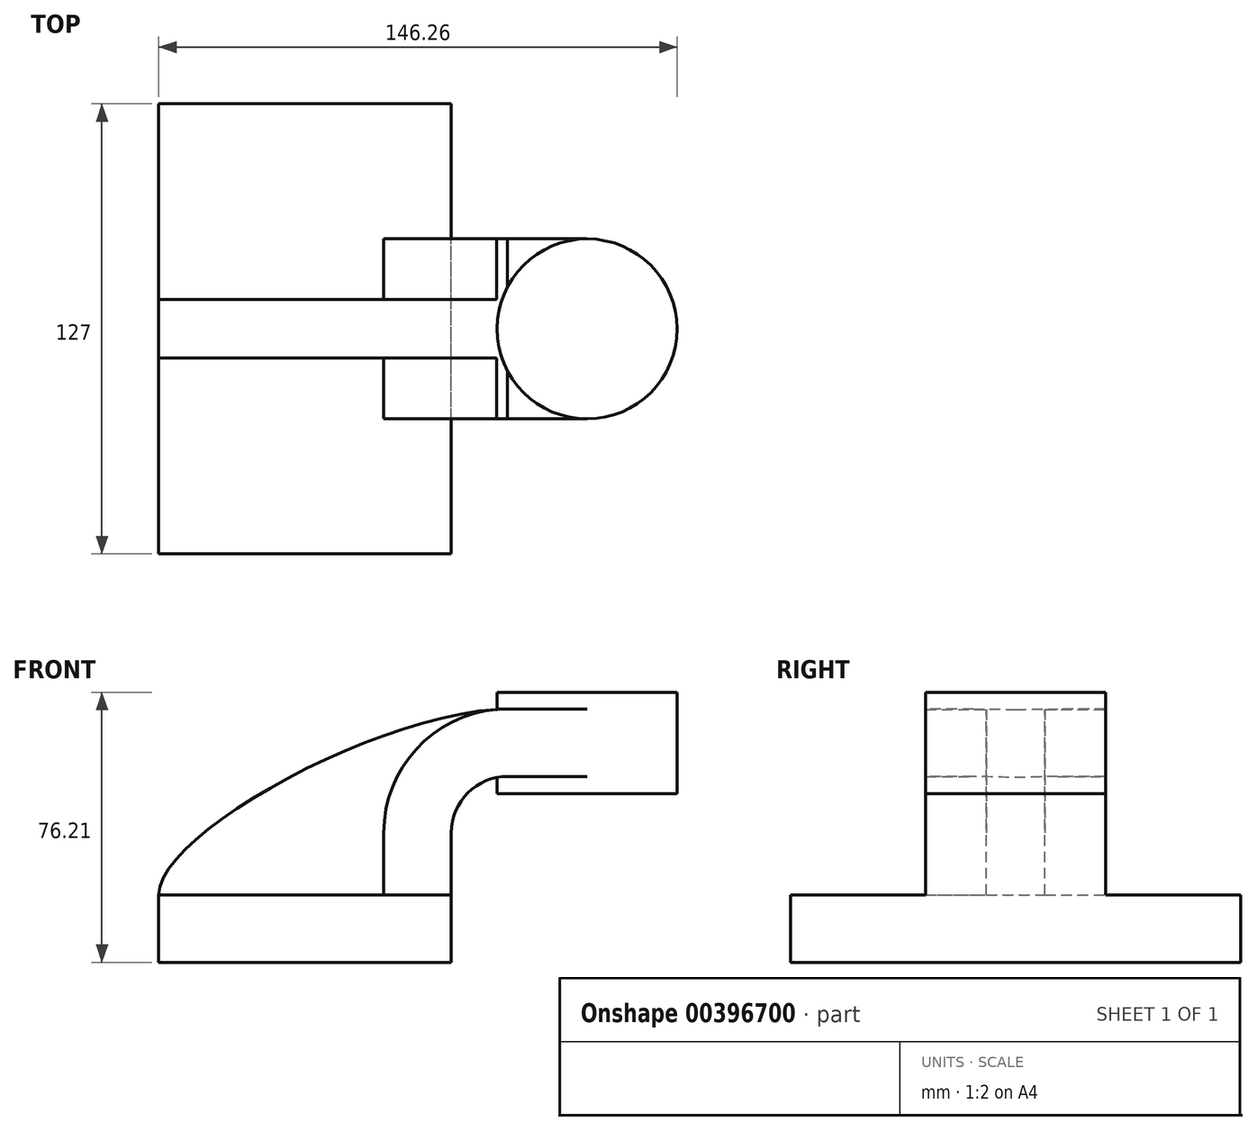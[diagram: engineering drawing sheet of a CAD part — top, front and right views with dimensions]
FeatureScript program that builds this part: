
annotation { "Feature Type Name" : "Feature", "Feature Type Description" : "" }
export const myFeature = defineFeature(function(context is Context, id is Id, definition is map)
    precondition{}
    {
        {
            var Q0;
            Q0=qCreatedBy(makeId("Front.planeOp"),FACE);
            var sketch = newSketch(context, id + "F0", { "sketchPlane" : qUnion([Q0])});
            skLineSegment(sketch, "E0.bottom", {"start": v(41.28, -9.52) * mm, "end": v(-41.27, -9.53) * mm});
            skLineSegment(sketch, "E0.top", {"start": v(41.27, 9.53) * mm, "end": v(-41.28, 9.53) * mm});
            skLineSegment(sketch, "E0.left", {"start": v(41.28, -9.52) * mm, "end": v(41.28, 9.53) * mm});
            skLineSegment(sketch, "E0.right", {"start": v(-41.27, -9.52) * mm, "end": v(-41.28, 9.53) * mm});
            skPoint(sketch, "E0.middle", {"position": v(0, 0) * mm});
            skLineSegment(sketch, "E1.bottom", {"start": v(104.98, 38.1) * mm, "end": v(54.18, 38.1) * mm});
            skLineSegment(sketch, "E1.top", {"start": v(104.98, 66.68) * mm, "end": v(54.18, 66.68) * mm});
            skLineSegment(sketch, "E1.left", {"start": v(104.98, 38.1) * mm, "end": v(104.98, 66.68) * mm});
            skLineSegment(sketch, "E1.right", {"start": v(54.18, 38.1) * mm, "end": v(54.18, 66.68) * mm});
            skPoint(sketch, "E1.middle", {"position": v(79.58, 52.39) * mm});
            skLineSegment(sketch, "E2", {"start": v(41.27, 9.53) * mm, "end": v(41.27, 27.05) * mm});
            skArc(sketch, "E3", {"start": v(41.27, 27.05) * mm, "mid": v(45.92, 38.28) * mm, "end": v(57.15, 42.93) * mm});
            skLineSegment(sketch, "E4", {"start": v(57.15, 42.93) * mm, "end": v(73.84, 42.93) * mm});
            skLineSegment(sketch, "E5", {"start": v(73.84, 42.93) * mm, "end": v(79.58, 42.93) * mm});
            skLineSegment(sketch, "E6.0", {"start": v(73.84, 61.98) * mm, "end": v(79.58, 61.98) * mm});
            skLineSegment(sketch, "E6.1", {"start": v(57.15, 61.98) * mm, "end": v(73.84, 61.98) * mm});
            skArc(sketch, "E6.2", {"start": v(22.23, 27.05) * mm, "mid": v(32.45, 51.75) * mm, "end": v(57.15, 61.98) * mm});
            skLineSegment(sketch, "E6.3", {"start": v(22.22, 9.53) * mm, "end": v(22.22, 27.05) * mm});
            skFitSpline(sketch, "E7", {"points": [v(-41.28, 9.53) * mm, v(57.15, 61.98) * mm], "startDerivative": vector(-0.54, 51.58) * mm, "endDerivative": vector(108.84, 2.1) * mm});
            skLineSegment(sketch, "E8", {"start": v(79.58, 61.98) * mm, "end": v(79.58, 38.1) * mm});
            skLineSegment(sketch, "E9", {"start": v(79.58, 61.98) * mm, "end": v(79.58, 66.68) * mm});
            skSolve(sketch);
        }
        {
            var Q0;
            Q0=makeQuery(id+"F0.imprint","IMPRINT",FACE,{"disambiguationData":[TD([[makeQuery(id+"F0.imprint","IMPRINT",EDGE,{"derivedFrom":sQuery(id+"F0.wireOp",EDGE,"E0.bottom")}),-1.0]])]});
            extrude(context, id + "F1", {"entities" : qUnion([Q0]), "endBound" : BoundingType.SYMMETRIC, "depth" : 127 * mm});
        }
        {
            var Q0;
            {var subQ1=sQuery(id+"F0.wireOp",EDGE,"E2");Q0=makeQuery(id+"F0.imprint","IMPRINT",FACE,{"disambiguationData":[TD([[makeQuery(id+"F0.imprint","IMPRINT",EDGE,{"derivedFrom":subQ1}),1.0]])]});}
            var Q1;
            {var subQ1=sQuery(id+"F0.wireOp",EDGE,"E4");Q1=makeQuery(id+"F0.imprint","IMPRINT",FACE,{"disambiguationData":[TD([[makeQuery(id+"F0.imprint","IMPRINT",EDGE,{"derivedFrom":subQ1}),1.0]])]});}
            extrude(context, id + "F2", {"entities" : qUnion([Q0, Q1]), "operationType" : NewBodyOperationType.ADD, "endBound" : BoundingType.SYMMETRIC, "depth" : 50.8 * mm});
        }
        {
            var Q0;
            {var subQ3=sQuery(id+"F0.wireOp",EDGE,"E6.3");Q0=makeQuery(id+"F0.imprint","IMPRINT",FACE,{"disambiguationData":[TD([[makeQuery(id+"F0.imprint","IMPRINT",EDGE,{"derivedFrom":subQ3}),1.0]])]});}
            extrude(context, id + "F3", {"entities" : qUnion([Q0]), "operationType" : NewBodyOperationType.ADD, "endBound" : BoundingType.SYMMETRIC, "depth" : 16.5 * mm});
        }
        {
            var Q0;
            {var subQ3=sQuery(id+"F0.wireOp",EDGE,"E1.left");Q0=makeQuery(id+"F0.imprint","IMPRINT",FACE,{"disambiguationData":[TD([[makeQuery(id+"F0.imprint","IMPRINT",EDGE,{"derivedFrom":subQ3}),1.0]])]});}
            var Q1;
            Q1=sQuery(id+"F0.wireOp",EDGE,"E8");
            revolve(context, id + "F4", {"operationType" : NewBodyOperationType.ADD, "entities" : qUnion([Q0]), "axis" : qUnion([Q1]), "revolveType" : RevolveType.FULL});
        }
    });
